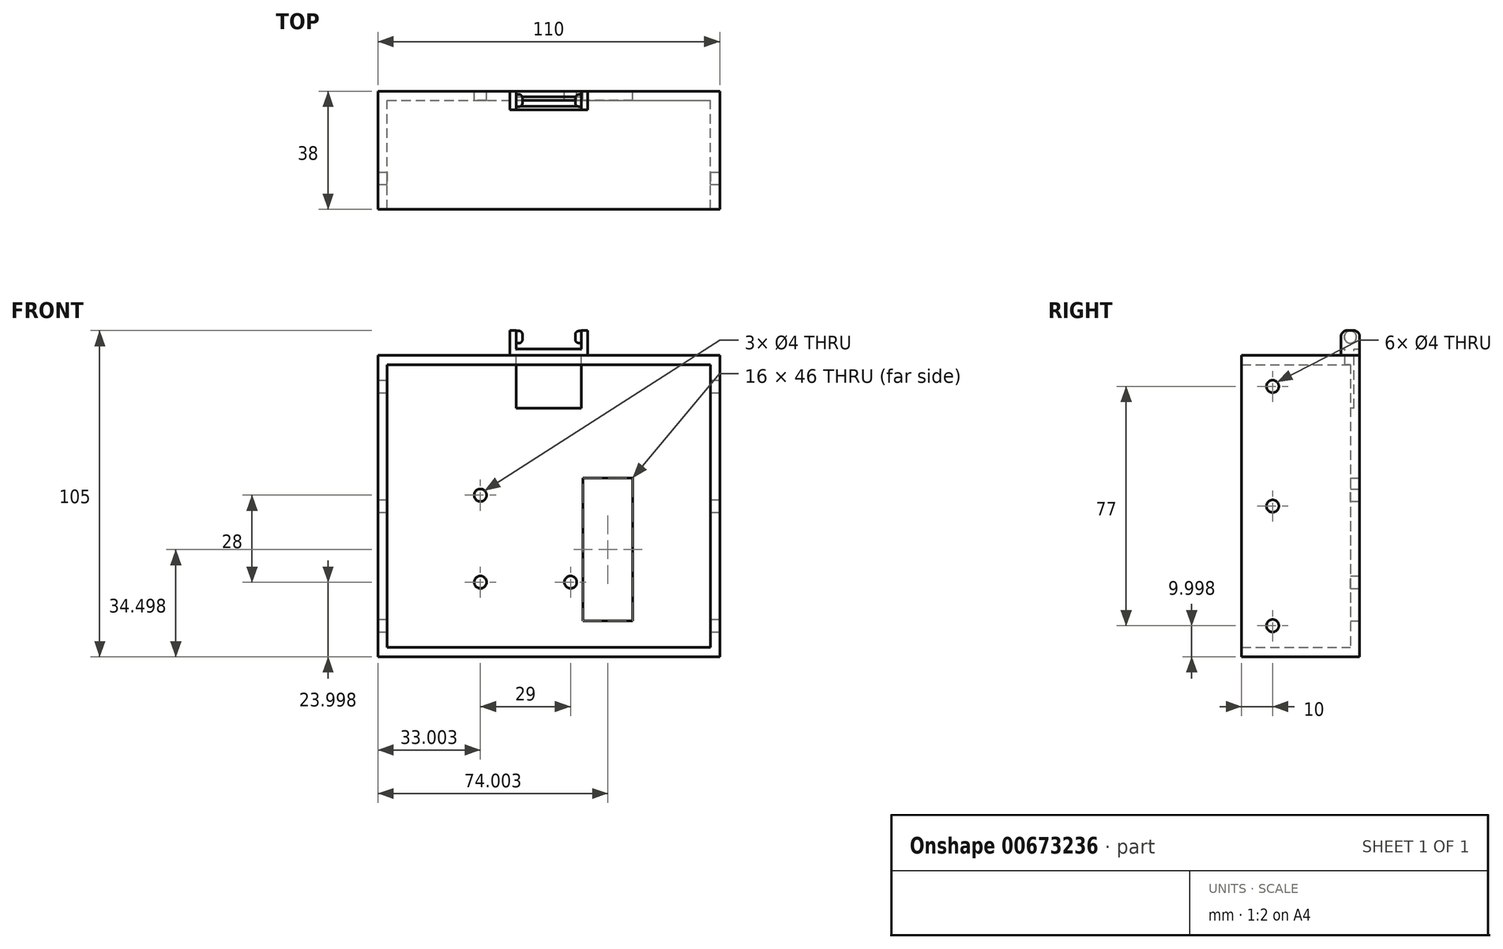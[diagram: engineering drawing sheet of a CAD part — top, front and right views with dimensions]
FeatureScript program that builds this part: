
annotation { "Feature Type Name" : "Feature", "Feature Type Description" : "" }
export const myFeature = defineFeature(function(context is Context, id is Id, definition is map)
    precondition{}
    {
        {
            var Q0;
            Q0=qCreatedBy(makeId("Front.planeOp"),FACE);
            var sketch = newSketch(context, id + "F0", { "sketchPlane" : qUnion([Q0])});
            skLineSegment(sketch, "E0.bottom", {"start": v(122.24, -21.81) * mm, "end": v(12.24, -21.81) * mm});
            skLineSegment(sketch, "E0.top", {"start": v(122.24, -118.81) * mm, "end": v(12.24, -118.81) * mm});
            skLineSegment(sketch, "E0.left", {"start": v(122.24, -21.81) * mm, "end": v(122.24, -118.81) * mm});
            skLineSegment(sketch, "E0.right", {"start": v(12.24, -21.81) * mm, "end": v(12.24, -118.81) * mm});
            skLineSegment(sketch, "E1.bottom", {"start": v(94.24, -61.31) * mm, "end": v(78.24, -61.31) * mm});
            skLineSegment(sketch, "E1.top", {"start": v(94.24, -107.31) * mm, "end": v(78.24, -107.31) * mm});
            skLineSegment(sketch, "E1.left", {"start": v(94.24, -61.31) * mm, "end": v(94.24, -107.31) * mm});
            skLineSegment(sketch, "E1.right", {"start": v(78.24, -61.31) * mm, "end": v(78.24, -107.31) * mm});
            skCircle(sketch, "E2", {"center": v(74.24, -94.81) * mm, "radius": 2 * mm});
            skCircle(sketch, "E3", {"center": v(45.24, -94.81) * mm, "radius": 2 * mm});
            skCircle(sketch, "E4", {"center": v(45.24, -66.81) * mm, "radius": 2 * mm});
            skSolve(sketch);
        }
        {
            var Q0;
            Q0 = qSketchRegion(id + "F0", true);
            extrude(context, id + "F1", {"entities" : qUnion([Q0]), "depth" : 3 * mm, "offsetDistance" : 25 * mm});
        }
        {
            var Q0;
            Q0=qCreatedBy(makeId("Front.planeOp"),FACE);
            var sketch = newSketch(context, id + "F2", { "sketchPlane" : qUnion([Q0])});
            skLineSegment(sketch, "E5.bottom", {"start": v(56.24, -24.81) * mm, "end": v(78.24, -24.81) * mm});
            skLineSegment(sketch, "E5.top", {"start": v(56.24, -26.41) * mm, "end": v(78.24, -26.41) * mm});
            skLineSegment(sketch, "E5.left", {"start": v(56.24, -24.81) * mm, "end": v(56.24, -26.41) * mm});
            skLineSegment(sketch, "E5.right", {"start": v(78.24, -24.81) * mm, "end": v(78.24, -26.41) * mm});
            skLineSegment(sketch, "E6.0", {"start": v(122.24, -21.81) * mm, "end": v(12.24, -21.81) * mm, "construction": true});
            skLineSegment(sketch, "E7", {"start": v(67.24, -21.81) * mm, "end": v(67.24, -24.81) * mm, "construction": true});
            skSolve(sketch);
        }
        {
            var Q0;
            Q0=makeQuery(id+"F2.imprint","IMPRINT",FACE,{"disambiguationData":[TD([[makeQuery(id+"F2.imprint","IMPRINT",EDGE,{"derivedFrom":sQuery(id+"F2.wireOp",EDGE,"E5.bottom")}),-1.0]])]});
            extrude(context, id + "F3", {"entities" : qUnion([Q0]), "operationType" : NewBodyOperationType.ADD, "depth" : 1.6 * mm, "offsetDistance" : 25 * mm});
        }
        {
            var Q0;
            Q0=makeQuery(id+"F1.opExtrude","CAP_FACE",FACE,{"disambiguationData":[OSD([sQuery(id+"F0.wireOp",EDGE,"E0.bottom"),sQuery(id+"F0.wireOp",EDGE,"E0.top"),sQuery(id+"F0.wireOp",EDGE,"E0.left"),sQuery(id+"F0.wireOp",EDGE,"E0.right"),sQuery(id+"F0.wireOp",EDGE,"E1.bottom"),sQuery(id+"F0.wireOp",EDGE,"E1.top"),sQuery(id+"F0.wireOp",EDGE,"E1.left"),sQuery(id+"F0.wireOp",EDGE,"E1.right"),sQuery(id+"F0.wireOp",EDGE,"E2"),sQuery(id+"F0.wireOp",EDGE,"E3"),sQuery(id+"F0.wireOp",EDGE,"E4")])],"isStart":false});
            var sketch = newSketch(context, id + "F4", { "sketchPlane" : qUnion([Q0])});
            skLineSegment(sketch, "E8.0", {"start": v(122.24, -21.81) * mm, "end": v(12.24, -21.81) * mm});
            skLineSegment(sketch, "E9.0", {"start": v(122.24, -118.81) * mm, "end": v(12.24, -118.81) * mm});
            skLineSegment(sketch, "E10.bottom", {"start": v(12.24, -21.81) * mm, "end": v(122.24, -21.81) * mm});
            skLineSegment(sketch, "E10.top", {"start": v(12.24, -118.81) * mm, "end": v(122.24, -118.81) * mm});
            skLineSegment(sketch, "E10.left", {"start": v(12.24, -21.81) * mm, "end": v(12.24, -118.81) * mm});
            skLineSegment(sketch, "E10.right", {"start": v(122.24, -21.81) * mm, "end": v(122.24, -118.81) * mm});
            skLineSegment(sketch, "E11.bottom", {"start": v(15.24, -24.81) * mm, "end": v(119.24, -24.81) * mm});
            skLineSegment(sketch, "E11.top", {"start": v(15.24, -115.81) * mm, "end": v(119.24, -115.81) * mm});
            skLineSegment(sketch, "E11.left", {"start": v(15.24, -24.81) * mm, "end": v(15.24, -115.81) * mm});
            skLineSegment(sketch, "E11.right", {"start": v(119.24, -24.81) * mm, "end": v(119.24, -115.81) * mm});
            skSolve(sketch);
        }
        {
            var Q0;
            Q0 = qSketchRegion(id + "F4", true);
            extrude(context, id + "F5", {"entities" : qUnion([Q0]), "operationType" : NewBodyOperationType.ADD, "depth" : 35 * mm, "offsetDistance" : 25 * mm});
        }
        {
            var Q0;
            Q0=makeQuery(id+"F5.boolean.opBoolean","MERGE",FACE,{"derivedFrom":[makeQuery(id+"F1.opExtrude","SWEPT_FACE",FACE,{"disambiguationData":[OSD([sQuery(id+"F0.wireOp",EDGE,"E0.bottom")])]}),makeQuery(id+"F5.opExtrude","SWEPT_FACE",FACE,{"disambiguationData":[OSD([sQuery(id+"F4.wireOp",EDGE,"E10.bottom")])]})]});
            var sketch = newSketch(context, id + "F6", { "sketchPlane" : qUnion([Q0])});
            skPoint(sketch, "E12.0", {"position": v(67.24, 0) * mm});
            skLineSegment(sketch, "E13.bottom", {"start": v(54.74, 0) * mm, "end": v(79.74, 0) * mm});
            skLineSegment(sketch, "E13.top", {"start": v(54.74, -6) * mm, "end": v(79.74, -6) * mm});
            skLineSegment(sketch, "E13.left", {"start": v(54.74, 0) * mm, "end": v(54.74, -6) * mm});
            skLineSegment(sketch, "E13.right", {"start": v(79.74, 0) * mm, "end": v(79.74, -6) * mm});
            skSolve(sketch);
        }
        {
            var Q0;
            Q0 = qSketchRegion(id + "F6", true);
            extrude(context, id + "F7", {"entities" : qUnion([Q0]), "operationType" : NewBodyOperationType.ADD, "depth" : 8 * mm, "offsetDistance" : 25 * mm});
        }
        {
            var Q0;
            Q0=makeQuery(id+"F7.opExtrude","CAP_FACE",FACE,{"disambiguationData":[OSD([sQuery(id+"F6.wireOp",EDGE,"E13.bottom"),sQuery(id+"F6.wireOp",EDGE,"E13.top"),sQuery(id+"F6.wireOp",EDGE,"E13.left"),sQuery(id+"F6.wireOp",EDGE,"E13.right")])],"isStart":false});
            var sketch = newSketch(context, id + "F8", { "sketchPlane" : qUnion([Q0])});
            skLineSegment(sketch, "E14.bottom", {"start": v(56.74, -1.8) * mm, "end": v(77.74, -1.8) * mm});
            skLineSegment(sketch, "E14.top", {"start": v(56.74, -4.8) * mm, "end": v(77.74, -4.8) * mm});
            skLineSegment(sketch, "E14.left", {"start": v(56.74, -1.8) * mm, "end": v(56.74, -4.8) * mm});
            skLineSegment(sketch, "E14.right", {"start": v(77.74, -1.8) * mm, "end": v(77.74, -4.8) * mm});
            skSolve(sketch);
        }
        {
            var Q0;
            Q0 = qSketchRegion(id + "F8", true);
            extrude(context, id + "F9", {"entities" : qUnion([Q0]), "operationType" : NewBodyOperationType.REMOVE, "oppositeDirection" : true, "depth" : 25 * mm, "offsetDistance" : 25 * mm});
        }
        {
            var Q0;
            Q0=makeQuery(id+"F7.opExtrude","SWEPT_FACE",FACE,{"disambiguationData":[OSD([sQuery(id+"F6.wireOp",EDGE,"E13.left")])]});
            var sketch = newSketch(context, id + "F10", { "sketchPlane" : qUnion([Q0])});
            skLineSegment(sketch, "E15.0", {"start": v(2, -13.81) * mm, "end": v(4, -13.81) * mm});
            skLineSegment(sketch, "E16.0", {"start": v(0, -15.81) * mm, "end": v(0, -21.81) * mm});
            skLineSegment(sketch, "E17.0", {"start": v(6, -15.81) * mm, "end": v(6, -21.81) * mm});
            skPoint(sketch, "E18.visualSharp", {"position": v(0, -13.81) * mm});
            skArc(sketch, "E18.filletArc", {"start": v(2, -13.81) * mm, "mid": v(0.59, -14.4) * mm, "end": v(0, -15.81) * mm});
            skPoint(sketch, "E19.visualSharp", {"position": v(6, -13.81) * mm});
            skArc(sketch, "E19.filletArc", {"start": v(6, -15.81) * mm, "mid": v(5.41, -14.4) * mm, "end": v(4, -13.81) * mm});
            skLineSegment(sketch, "E20", {"start": v(4, -13.81) * mm, "end": v(6, -13.81) * mm});
            skLineSegment(sketch, "E21", {"start": v(6, -15.81) * mm, "end": v(6, -13.81) * mm});
            skLineSegment(sketch, "E22", {"start": v(0, -15.81) * mm, "end": v(0, -13.81) * mm});
            skSolve(sketch);
        }
        {
            var Q0;
            {var subQ0=sQuery(id+"F10.wireOp",EDGE,"E18.filletArc");Q0=makeQuery(id+"F10.imprint","IMPRINT",FACE,{"disambiguationData":[TD([[makeQuery(id+"F10.imprint","IMPRINT",EDGE,{"derivedFrom":subQ0}),-1.0]])]});}
            var Q1;
            Q1=makeQuery(id+"F10.imprint","IMPRINT",FACE,{"disambiguationData":[TD([[makeQuery(id+"F10.imprint","IMPRINT",EDGE,{"derivedFrom":sQuery(id+"F10.wireOp",EDGE,"E19.filletArc")}),-1.0]])]});
            extrude(context, id + "F11", {"entities" : qUnion([Q0, Q1]), "operationType" : NewBodyOperationType.REMOVE, "oppositeDirection" : true, "depth" : 25 * mm, "offsetDistance" : 25 * mm});
        }
        {
            var Q0;
            Q0=makeQuery(id+"F7.boolean.opBoolean","MERGE",FACE,{"derivedFrom":[makeQuery(id+"F1.opExtrude","CAP_FACE",FACE,{"disambiguationData":[OSD([sQuery(id+"F0.wireOp",EDGE,"E0.bottom"),sQuery(id+"F0.wireOp",EDGE,"E0.top"),sQuery(id+"F0.wireOp",EDGE,"E0.left"),sQuery(id+"F0.wireOp",EDGE,"E0.right"),sQuery(id+"F0.wireOp",EDGE,"E1.bottom"),sQuery(id+"F0.wireOp",EDGE,"E1.top"),sQuery(id+"F0.wireOp",EDGE,"E1.left"),sQuery(id+"F0.wireOp",EDGE,"E1.right"),sQuery(id+"F0.wireOp",EDGE,"E2"),sQuery(id+"F0.wireOp",EDGE,"E3"),sQuery(id+"F0.wireOp",EDGE,"E4")])],"isStart":true}),makeQuery(id+"F7.opExtrude","SWEPT_FACE",FACE,{"disambiguationData":[OSD([sQuery(id+"F6.wireOp",EDGE,"E13.bottom")])]})]});
            var sketch = newSketch(context, id + "F12", { "sketchPlane" : qUnion([Q0])});
            skPoint(sketch, "E23.0", {"position": v(-77.74, -13.81) * mm});
            skPoint(sketch, "E24.0", {"position": v(-56.74, -13.81) * mm});
            skPoint(sketch, "E25.0", {"position": v(-54.74, -21.81) * mm});
            skPoint(sketch, "E26.0", {"position": v(-79.74, -21.81) * mm});
            skLineSegment(sketch, "E27.bottom", {"start": v(-77.74, -13.81) * mm, "end": v(-56.74, -13.81) * mm});
            skLineSegment(sketch, "E27.top", {"start": v(-77.74, -19.81) * mm, "end": v(-56.74, -19.81) * mm});
            skLineSegment(sketch, "E27.left", {"start": v(-77.74, -13.81) * mm, "end": v(-77.74, -19.81) * mm});
            skLineSegment(sketch, "E27.right", {"start": v(-56.74, -13.81) * mm, "end": v(-56.74, -19.81) * mm});
            skSolve(sketch);
        }
        {
            var Q0;
            Q0 = qSketchRegion(id + "F12", true);
            extrude(context, id + "F13", {"entities" : qUnion([Q0]), "operationType" : NewBodyOperationType.REMOVE, "oppositeDirection" : true, "depth" : 7 * mm, "offsetDistance" : 25 * mm});
        }
        {
            var Q0;
            Q0=makeQuery(id+"F13.boolean.opBoolean","MERGE",FACE,{"derivedFrom":[makeQuery(id+"F9.boolean.opBoolean","COPY",FACE,{"derivedFrom":makeQuery(id+"F9.opExtrude","SWEPT_FACE",FACE,{"disambiguationData":[OSD([sQuery(id+"F8.wireOp",EDGE,"E14.right")])]})}),makeQuery(id+"F13.opExtrude","SWEPT_FACE",FACE,{"disambiguationData":[OSD([sQuery(id+"F12.wireOp",EDGE,"E27.left")])]})]});
            var sketch = newSketch(context, id + "F14", { "sketchPlane" : qUnion([Q0])});
            skCircle(sketch, "E28", {"center": v(3, -15.91) * mm, "radius": 1.95 * mm});
            skLineSegment(sketch, "E29.0", {"start": v(2, -13.81) * mm, "end": v(4, -13.81) * mm});
            skLineSegment(sketch, "E30", {"start": v(3, -15.91) * mm, "end": v(3, -13.81) * mm});
            skSolve(sketch);
        }
        {
            var Q0;
            Q0=makeQuery(id+"F14.imprint","IMPRINT",FACE,{"disambiguationData":[TD([[makeQuery(id+"F14.imprint","IMPRINT",EDGE,{"derivedFrom":sQuery(id+"F14.wireOp",EDGE,"E28")}),1.0]])]});
            extrude(context, id + "F15", {"entities" : qUnion([Q0]), "operationType" : NewBodyOperationType.ADD, "depth" : 2 * mm, "offsetDistance" : 25 * mm});
        }
        {
            var Q0;
            Q0=makeQuery(id+"F15.opExtrude","CAP_EDGE",EDGE,{"disambiguationData":[OSD([sQuery(id+"F14.wireOp",EDGE,"E28")])],"isStart":false});
            fillet(context, id + "F16", {"entities" : qUnion([Q0]), "radius" : 1.2 * mm, "tangentPropagation" : true, "allowEdgeOverflow" : false});
        }
        {
            var Q0;
            Q0=makeQuery(id+"F13.boolean.opBoolean","MERGE",FACE,{"derivedFrom":[makeQuery(id+"F9.boolean.opBoolean","COPY",FACE,{"derivedFrom":makeQuery(id+"F9.opExtrude","SWEPT_FACE",FACE,{"disambiguationData":[OSD([sQuery(id+"F8.wireOp",EDGE,"E14.left")])]})}),makeQuery(id+"F13.opExtrude","SWEPT_FACE",FACE,{"disambiguationData":[OSD([sQuery(id+"F12.wireOp",EDGE,"E27.right")])]})]});
            var sketch = newSketch(context, id + "F17", { "sketchPlane" : qUnion([Q0])});
            skLineSegment(sketch, "E31.0", {"start": v(-2, -13.81) * mm, "end": v(-4, -13.81) * mm});
            skLineSegment(sketch, "E32", {"start": v(-3, -13.81) * mm, "end": v(-3, -15.91) * mm});
            skCircle(sketch, "E33", {"center": v(-3, -15.91) * mm, "radius": 2 * mm});
            skSolve(sketch);
        }
        {
            var Q0;
            Q0 = qSketchRegion(id + "F17", true);
            extrude(context, id + "F18", {"entities" : qUnion([Q0]), "operationType" : NewBodyOperationType.ADD, "depth" : 2 * mm, "offsetDistance" : 25 * mm});
        }
        {
            var Q0;
            Q0=makeQuery(id+"F18.opExtrude","CAP_EDGE",EDGE,{"disambiguationData":[OSD([sQuery(id+"F17.wireOp",EDGE,"E33")])],"isStart":false});
            fillet(context, id + "F19", {"entities" : qUnion([Q0]), "radius" : 1.2 * mm, "tangentPropagation" : true, "allowEdgeOverflow" : false});
        }
        {
            var Q0;
            Q0=makeQuery(id+"F5.boolean.opBoolean","MERGE",FACE,{"derivedFrom":[makeQuery(id+"F1.opExtrude","SWEPT_FACE",FACE,{"disambiguationData":[OSD([sQuery(id+"F0.wireOp",EDGE,"E0.left")])]}),makeQuery(id+"F5.opExtrude","SWEPT_FACE",FACE,{"disambiguationData":[OSD([sQuery(id+"F4.wireOp",EDGE,"E10.right")])]})]});
            var sketch = newSketch(context, id + "F20", { "sketchPlane" : qUnion([Q0])});
            skLineSegment(sketch, "E34", {"start": v(-28, -31.81) * mm, "end": v(-28, -108.81) * mm, "construction": true});
            skCircle(sketch, "E35", {"center": v(-28, -31.81) * mm, "radius": 2 * mm});
            skCircle(sketch, "E36", {"center": v(-28, -108.81) * mm, "radius": 2 * mm});
            skCircle(sketch, "E37", {"center": v(-28, -70.31) * mm, "radius": 2 * mm});
            skSolve(sketch);
        }
        {
            var Q0;
            Q0 = qSketchRegion(id + "F20", true);
            extrude(context, id + "F21", {"entities" : qUnion([Q0]), "operationType" : NewBodyOperationType.REMOVE, "endBound" : BoundingType.THROUGH_ALL, "oppositeDirection" : true, "depth" : 25 * mm, "offsetDistance" : 25 * mm});
        }
    });
